# Revit family: Toilet_Tissue_Dispenser-Bradley_Corp-5126
name_source: partatom
category: Specialty Equipment
revit_build: Autodesk Revit MEP 2012 (Build: 20110309_2315(x64)
units: mm (PartAtom-declared; Revit-internal decimal feet)

## types (2) — shared parameters
ADA Compliant = Yes
Assembly Code = C1030200
Buy American Act = To Be Determined
Default Elevation = 48 "
Depth = 2 "
Description = Toilet Tissue Dispenser
Height = 6.375 "
Low Emitting Material = No
Manufacturer = Bradley Corporation
MasterFormat Number = 10 28 00
MasterFormat Title = Toilet, Bath, and Laundry Accessories
OmniClass Table 21 Number = 21-03 10 90 40
OmniClass Table 21 Title = Toilet, Bath, and Laundry Accessories
OmniClass Table 23 Number = 23.31.25.21
OmniClass Table 23 Title = Toilet Paper Dispensers
Product Tech Data URL - English = http://bradleycorp.com
Specifications URL = http://www.bradleycorp.com
URL = http://www.bradleycorp.com
Unit Material = Metal - Bradley Corp - Stainless Steel - Bright Polish
Version = 2.0
Warranty Information = Complete Unit 1 Year Warranty. This Warranty does not cover installation or any other labor charges and does not apply to any units which have been damaged by abuse, improper installation, imporper maintanence, or altered in any way.
Width = 12.625 "
zero-valued in all types: Percentage of Recycled Content

## per-type parameters (varying)
| type | Spindle Material | Type Comments |
| 5126 | Plastic - Bradley Corp - Chrome | Bright Finish Stainless Steel |
| 5126-52 | Plastic - Bradley Corp - White | Bright Finish Stainless Steel, Anti-Theft Spindle |

note: column(s) folded — value = type name in every type: Model

## geometry (parser evidence)
native form markers: Blend x8, Sweep x1
no freeform markers — native parametric forms only
